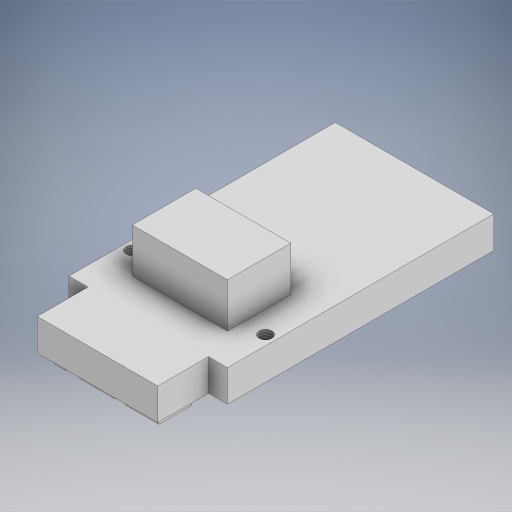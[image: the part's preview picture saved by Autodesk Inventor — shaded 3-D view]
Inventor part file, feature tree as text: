
AUTODESK INVENTOR PART (.ipt)
format: ipt  version: 2023 (Build 270158000, 158)  size: 393,216 bytes
history: native  units: mm
features: extrude x4, sketch x4, thread x2
ambient origin geometry x8: Origin, YZ Plane, XZ Plane, XY Plane, X Axis, Y Axis, Z Axis, Center Point
bodies: Solid1 (feature_tree)
feature tree (10):
  extrude  "Extrusion1"  Depth=3.0mm
  extrude  "Extrusion2"  Depth=42.0mm
  extrude  "Extrusion3"  Depth=5.0mm TaperAngle=0.0deg
  thread  "Thread1"  [1 undecoded]
  thread  "Thread2"  [1 undecoded]
  extrude  "Extrusion4"  Depth=2.0mm
  sketch  "Sketch1"  dims[d0=19.0mm d1=3.0mm]
  sketch  "Sketch2"  dims[d2=3.0mm d3=42.0mm]
  sketch  "Sketch3"  dims[d4=25.0mm d5=5.0mm d6=0.0mm d7=5.0mm d8=10.0mm]
  sketch  "Sketch4"  dims[d11=7.0mm d12=0.0mm d13=2.0mm d14=7.5mm d15=1.5mm d16=2.0mm d17=8.5mm d18=1.5mm d19=7.0mm d20=0.0mm d21=7.0mm d22=0.0mm d23=7.0mm d24=0.0mm d25=5.0mm d26=5.0mm d27=8.0mm d28=1.0mm d29=0.0mm]
note: 2 required parameter values undecoded (feature->parameter linkage not recoverable at this tier; creation-order binding heuristic only, values carry confidence <= 0.55)
